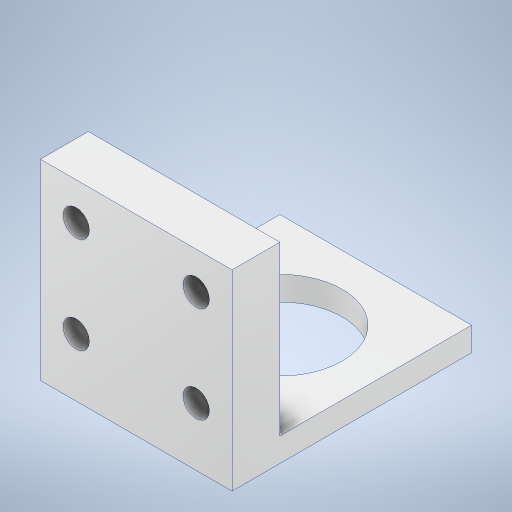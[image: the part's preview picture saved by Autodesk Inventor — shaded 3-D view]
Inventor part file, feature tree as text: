
AUTODESK INVENTOR PART (.ipt)
format: ipt  version: 2023 (Build 270158000, 158)  size: 267,776 bytes
history: native  units: mm
features: sketch x4, extrude x2, hole x2, other x1
ambient origin geometry x8: Origin, YZ Plane, XZ Plane, XY Plane, X Axis, Y Axis, Z Axis, Center Point
bodies: Body1 (feature_tree)
feature tree (9):
  other  "Sólido1"
  extrude  "Extrusão1"  Depth=50.0mm
  extrude  "Extrusão2"  Depth=10.0mm
  hole  "Furo1"  [1 undecoded]
  hole  "Hole2"  [1 undecoded]
  sketch  "Esboço1"  dims[d0=40.0mm d1=50.0mm]
  sketch  "Esboço2"  dims[d2=5.0mm d3=0.0mm d4=10.0mm]
  sketch  "Esboço3"  dims[d5=35.0mm d6=0.0mm d7=40.0mm]
  sketch  "Sketch4"  dims[d8=40.0mm d9=20.0mm d10=20.0mm d11=26.0mm d12=6.0mm d13=4.0mm d14=2.0mm d15=90.0deg d16=0.5mm d17=20.594885mm d18=20.0mm d20=20.1mm d21=20.0mm d23=25.05mm d26=7.75mm d27=40.0mm d28=7.475mm d29=5.5mm d30=4.0mm d31=4.0mm d32=2.0mm d33=90.0deg d34=0.5mm d35=20.594885mm]
note: 2 required parameter values undecoded (feature->parameter linkage not recoverable at this tier; creation-order binding heuristic only, values carry confidence <= 0.55)
